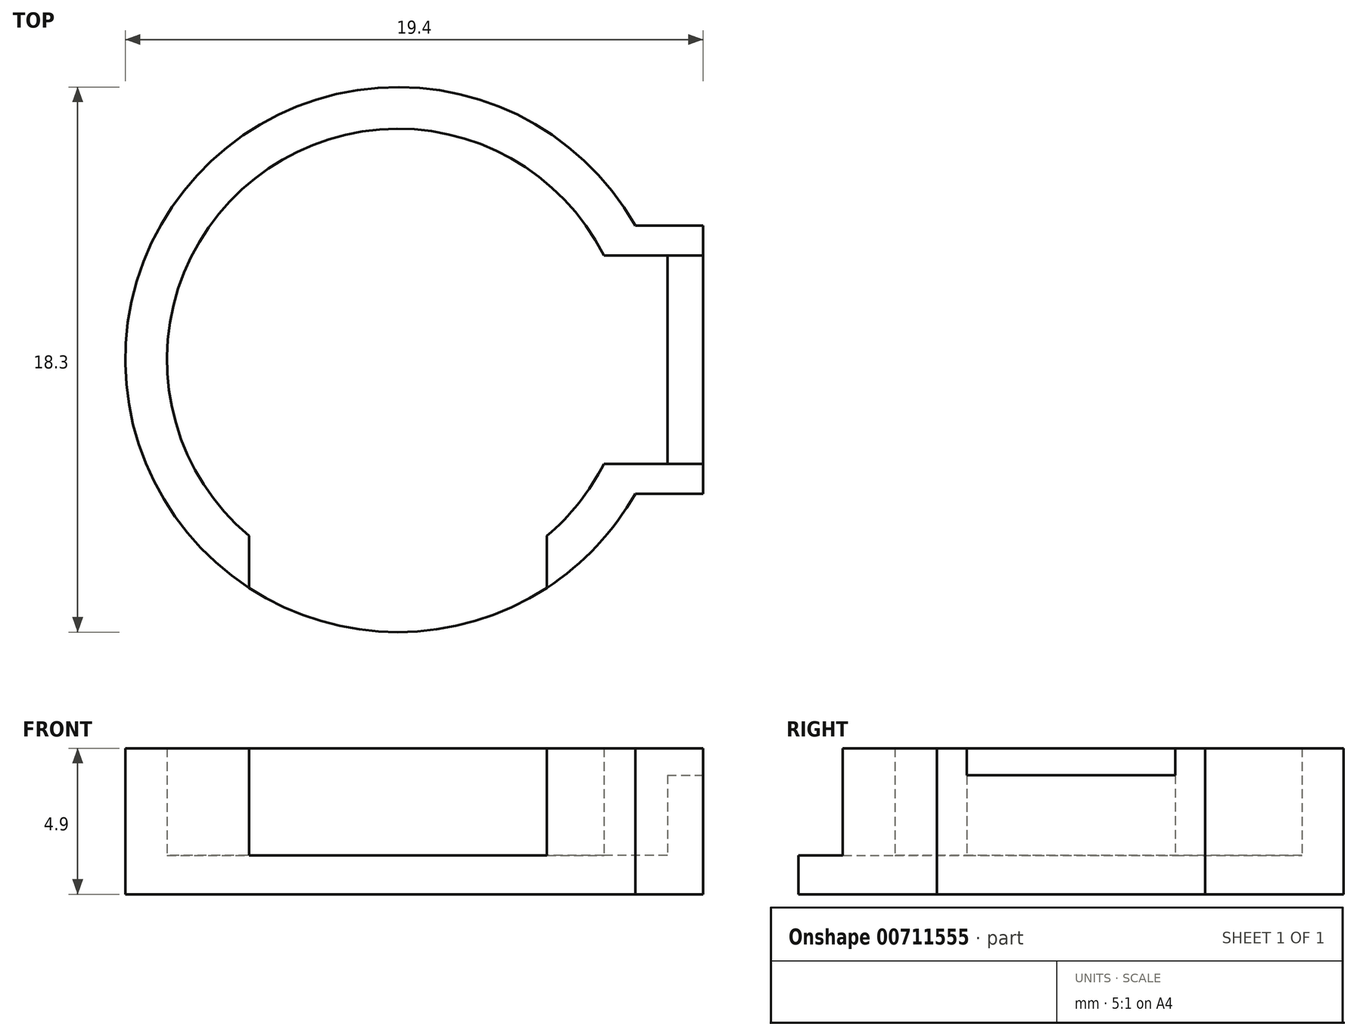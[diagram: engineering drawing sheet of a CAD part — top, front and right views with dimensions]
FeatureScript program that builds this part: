
annotation { "Feature Type Name" : "Feature", "Feature Type Description" : "" }
export const myFeature = defineFeature(function(context is Context, id is Id, definition is map)
    precondition{}
    {
        {
            var Q0;
            Q0=qCreatedBy(makeId("Top.planeOp"),FACE);
            var sketch = newSketch(context, id + "F0", { "sketchPlane" : qUnion([Q0])});
            skArc(sketch, "E0", {"start": v(6.91, 3.5) * mm, "mid": v(-7.75, 0) * mm, "end": v(6.91, -3.5) * mm});
            skLineSegment(sketch, "E1.bottom", {"start": v(9.05, 3.5) * mm, "end": v(6.45, 3.5) * mm});
            skLineSegment(sketch, "E1.top", {"start": v(9.05, -3.5) * mm, "end": v(6.45, -3.5) * mm});
            skLineSegment(sketch, "E1.left", {"start": v(9.05, 3.5) * mm, "end": v(9.05, -3.5) * mm});
            skPoint(sketch, "E1.middle", {"position": v(7.75, 0) * mm});
            skLineSegment(sketch, "E2", {"start": v(-7.75, 0) * mm, "end": v(-7.75, -7.8) * mm, "construction": true});
            skLineSegment(sketch, "E3", {"start": v(6.91, -3.5) * mm, "end": v(6.45, -3.5) * mm});
            skLineSegment(sketch, "E4", {"start": v(6.91, 3.5) * mm, "end": v(6.45, 3.5) * mm});
            skArc(sketch, "E5", {"start": v(7.97, 4.5) * mm, "mid": v(-9.15, 0) * mm, "end": v(7.97, -4.5) * mm});
            skLineSegment(sketch, "E6", {"start": v(7.97, 4.5) * mm, "end": v(10.25, 4.5) * mm});
            skLineSegment(sketch, "E7", {"start": v(10.25, 4.5) * mm, "end": v(10.25, -4.5) * mm});
            skLineSegment(sketch, "E8", {"start": v(10.25, -4.5) * mm, "end": v(7.97, -4.5) * mm});
            skLineSegment(sketch, "E9", {"start": v(-5, -5.92) * mm, "end": v(-5, -7.66) * mm});
            skLineSegment(sketch, "E10", {"start": v(5, -5.92) * mm, "end": v(5, -7.66) * mm});
            skLineSegment(sketch, "E11", {"start": v(9.05, 3.5) * mm, "end": v(10.25, 3.5) * mm});
            skLineSegment(sketch, "E12", {"start": v(9.05, -3.5) * mm, "end": v(10.25, -3.5) * mm});
            skSolve(sketch);
        }
        {
            var Q0;
            Q0 = qSketchRegion(id + "F0", true);
            var Q1;
            Q1=makeQuery(id+"F0.imprint","IMPRINT",FACE,{"disambiguationData":[TD([[makeQuery(id+"F0.imprint","IMPRINT",EDGE,{"derivedFrom":sQuery(id+"F0.wireOp",EDGE,"E1.bottom")}),1.0]])]});
            extrude(context, id + "F1", {"entities" : qUnion([Q0, Q1]), "depth" : 1.3 * mm, "offsetDistance" : 25 * mm});
        }
        {
            var Q0;
            Q0=makeQuery(id+"F0.imprint","IMPRINT",FACE,{"disambiguationData":[TD([[makeQuery(id+"F0.imprint","IMPRINT",EDGE,{"derivedFrom":sQuery(id+"F0.wireOp",EDGE,"E1.bottom")}),-1.0]])]});
            var Q1;
            Q1=makeQuery(id+"F0.imprint","IMPRINT",FACE,{"disambiguationData":[TD([[makeQuery(id+"F0.imprint","IMPRINT",EDGE,{"derivedFrom":sQuery(id+"F0.wireOp",EDGE,"E1.top")}),1.0]])]});
            extrude(context, id + "F2", {"entities" : qUnion([Q0, Q1]), "operationType" : NewBodyOperationType.ADD, "depth" : 4.9 * mm, "offsetDistance" : 25 * mm});
        }
        {
            var Q0;
            Q0=makeQuery(id+"F0.imprint","IMPRINT",FACE,{"disambiguationData":[TD([[makeQuery(id+"F0.imprint","IMPRINT",EDGE,{"derivedFrom":sQuery(id+"F0.wireOp",EDGE,"E1.left")}),1.0]])]});
            extrude(context, id + "F3", {"entities" : qUnion([Q0]), "operationType" : NewBodyOperationType.ADD, "depth" : 4 * mm, "offsetDistance" : 25 * mm});
        }
    });
